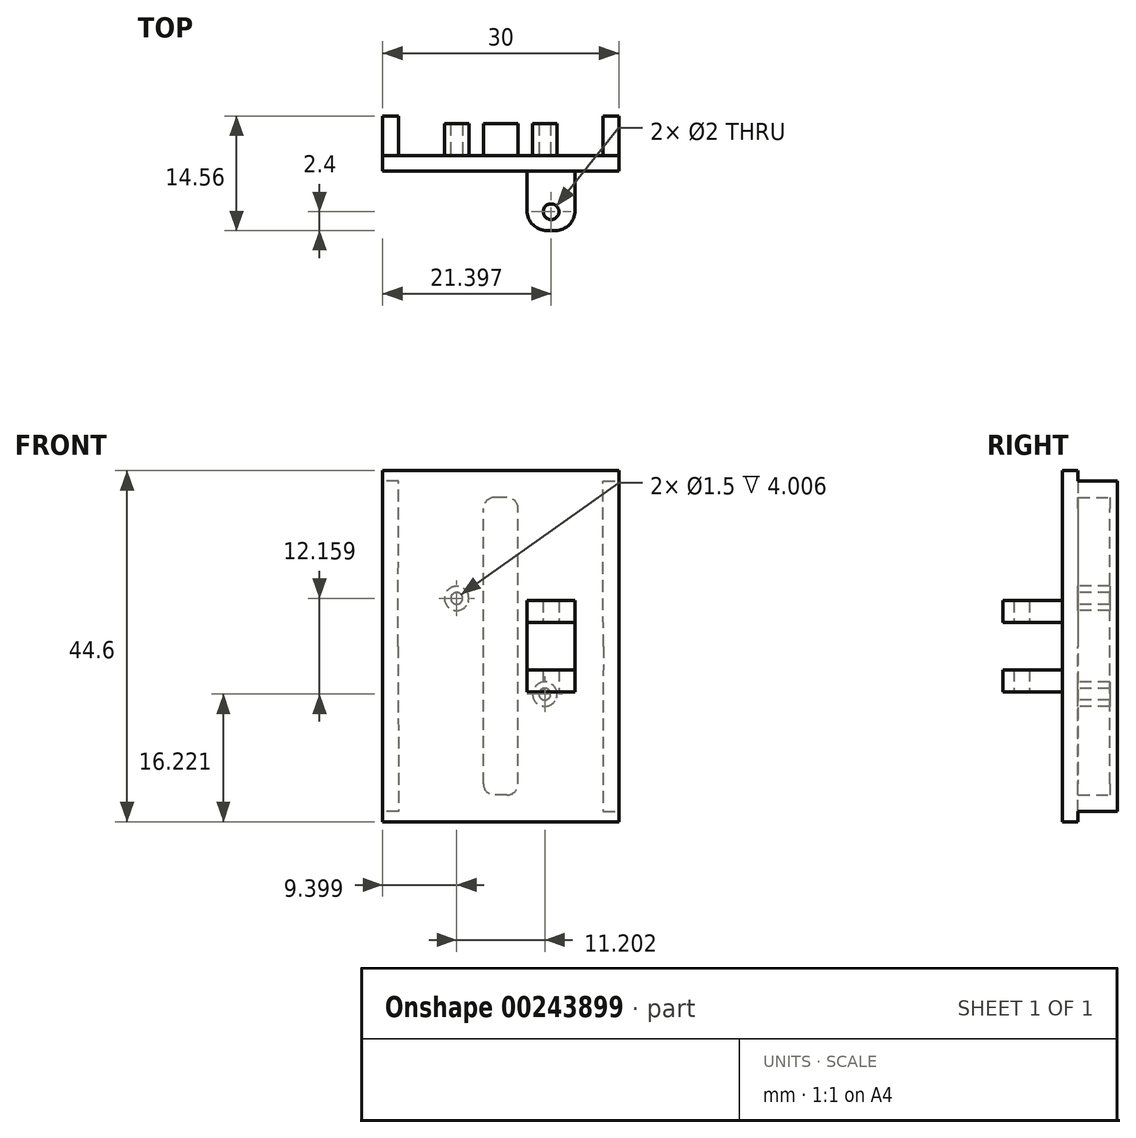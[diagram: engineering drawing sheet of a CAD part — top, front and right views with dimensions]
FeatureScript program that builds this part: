
annotation { "Feature Type Name" : "Feature", "Feature Type Description" : "" }
export const myFeature = defineFeature(function(context is Context, id is Id, definition is map)
    precondition{}
    {
        {
            var Q0;
            Q0=qCreatedBy(makeId("Front.planeOp"),FACE);
            var sketch = newSketch(context, id + "F0", { "sketchPlane" : qUnion([Q0])});
            skLineSegment(sketch, "E0.bottom", {"start": v(15, 22.3) * mm, "end": v(-15, 22.3) * mm});
            skLineSegment(sketch, "E0.top", {"start": v(15, -22.3) * mm, "end": v(-15, -22.3) * mm});
            skLineSegment(sketch, "E0.left", {"start": v(15, 22.3) * mm, "end": v(15, -22.3) * mm});
            skLineSegment(sketch, "E0.right", {"start": v(-15, 22.3) * mm, "end": v(-15, -22.3) * mm});
            skSolve(sketch);
        }
        {
            var Q0;
            Q0=makeQuery(id+"F0.imprint","IMPRINT",FACE,{"disambiguationData":[TD([[makeQuery(id+"F0.imprint","IMPRINT",EDGE,{"derivedFrom":sQuery(id+"F0.wireOp",EDGE,"E0.bottom")}),1.0]])]});
            extrude(context, id + "F1", {"entities" : qUnion([Q0]), "depth" : 8 * mm});
        }
        {
            var Q0;
            Q0=makeQuery(id+"F0.imprint","IMPRINT",FACE,{"disambiguationData":[TD([[makeQuery(id+"F0.imprint","IMPRINT",EDGE,{"derivedFrom":sQuery(id+"F0.wireOp",EDGE,"E0.bottom")}),1.0]])]});
            var sketch = newSketch(context, id + "F2", { "sketchPlane" : qUnion([Q0])});
            skLineSegment(sketch, "E1.0", {"start": v(15, 22.3) * mm, "end": v(0, 22.3) * mm});
            skLineSegment(sketch, "E2.0", {"start": v(15, 22.3) * mm, "end": v(15, 20.99) * mm});
            skLineSegment(sketch, "E3.top", {"start": v(15, 20.99) * mm, "end": v(13, 20.99) * mm});
            skPoint(sketch, "E4", {"position": v(15, 20.99) * mm});
            skLineSegment(sketch, "E5", {"start": v(13, 20.99) * mm, "end": v(13.02, 0) * mm});
            skLineSegment(sketch, "E6.bottom", {"start": v(-0.8, 18.9) * mm, "end": v(0.8, 18.9) * mm});
            skLineSegment(sketch, "E6.top", {"start": v(-0.8, -18.9) * mm, "end": v(0.8, -18.9) * mm});
            skLineSegment(sketch, "E6.left", {"start": v(-2.2, 17.5) * mm, "end": v(-2.2, -17.5) * mm});
            skLineSegment(sketch, "E6.right", {"start": v(2.2, 17.5) * mm, "end": v(2.2, -17.5) * mm});
            skPoint(sketch, "E6.middle", {"position": v(0, 0) * mm});
            skPoint(sketch, "E7.visualSharp", {"position": v(2.2, 18.9) * mm});
            skArc(sketch, "E7.filletArc", {"start": v(2.2, 17.5) * mm, "mid": v(1.8, 18.5) * mm, "end": v(0.8, 18.9) * mm});
            skPoint(sketch, "E8.visualSharp", {"position": v(-2.2, 18.9) * mm});
            skArc(sketch, "E8.filletArc", {"start": v(-0.8, 18.9) * mm, "mid": v(-1.8, 18.5) * mm, "end": v(-2.2, 17.5) * mm});
            skPoint(sketch, "E9.visualSharp", {"position": v(2.2, -18.9) * mm});
            skArc(sketch, "E9.filletArc", {"start": v(0.8, -18.9) * mm, "mid": v(1.8, -18.5) * mm, "end": v(2.2, -17.5) * mm});
            skPoint(sketch, "E10.visualSharp", {"position": v(-2.2, -18.9) * mm});
            skArc(sketch, "E10.filletArc", {"start": v(-2.2, -17.5) * mm, "mid": v(-1.8, -18.5) * mm, "end": v(-0.8, -18.9) * mm});
            skLineSegment(sketch, "E11.MirrorCS", {"start": v(-15, 22.3) * mm, "end": v(0, 22.3) * mm});
            skLineSegment(sketch, "E12.MirrorCS", {"start": v(-13, 20.99) * mm, "end": v(-13.02, 0) * mm});
            skLineSegment(sketch, "E13.MirrorCS", {"start": v(-15, 22.3) * mm, "end": v(-15, 20.99) * mm});
            skLineSegment(sketch, "E14.MirrorCS", {"start": v(-15, 20.99) * mm, "end": v(-13, 20.99) * mm});
            skLineSegment(sketch, "E15.MirrorCS", {"start": v(13, -20.99) * mm, "end": v(13.02, 0) * mm});
            skLineSegment(sketch, "E16.MirrorCS", {"start": v(15, -20.99) * mm, "end": v(13, -20.99) * mm});
            skLineSegment(sketch, "E17.MirrorCS", {"start": v(15, -22.3) * mm, "end": v(0, -22.3) * mm});
            skLineSegment(sketch, "E18.MirrorCS", {"start": v(-15, -22.3) * mm, "end": v(0, -22.3) * mm});
            skLineSegment(sketch, "E19.MirrorCS", {"start": v(-13, -20.99) * mm, "end": v(-13.02, 0) * mm});
            skLineSegment(sketch, "E20.MirrorCS", {"start": v(-15, -20.99) * mm, "end": v(-13, -20.99) * mm});
            skLineSegment(sketch, "E21.MirrorCS", {"start": v(-15, -22.3) * mm, "end": v(-15, -20.99) * mm});
            skLineSegment(sketch, "E22.MirrorCS", {"start": v(15, -22.3) * mm, "end": v(15, -20.99) * mm});
            skSolve(sketch);
        }
        {
            var Q0;
            Q0=makeQuery(id+"F2.imprint","IMPRINT",FACE,{"disambiguationData":[TD([[makeQuery(id+"F2.imprint","IMPRINT",EDGE,{"derivedFrom":sQuery(id+"F2.wireOp",EDGE,"E1.0")}),1.0]])]});
            extrude(context, id + "F3", {"entities" : qUnion([Q0]), "operationType" : NewBodyOperationType.REMOVE, "depth" : 6 * mm});
        }
        {
            var Q0;
            Q0=qCreatedBy(makeId("Top.planeOp"),FACE);
            var sketch = newSketch(context, id + "F4", { "sketchPlane" : qUnion([Q0])});
            skLineSegment(sketch, "E23.bottom", {"start": v(10.41, 0) * mm, "end": v(-10.59, 0) * mm});
            skLineSegment(sketch, "E23.top", {"start": v(10.41, -2) * mm, "end": v(-10.59, -2) * mm});
            skLineSegment(sketch, "E23.left", {"start": v(10.41, 0) * mm, "end": v(10.41, -2) * mm});
            skLineSegment(sketch, "E23.right", {"start": v(-10.59, 0) * mm, "end": v(-10.59, -2) * mm});
            skSolve(sketch);
        }
        {
            var Q0;
            Q0=makeQuery(id+"F1.opExtrude","CAP_FACE",FACE,{"disambiguationData":[OSD([sQuery(id+"F0.wireOp",EDGE,"E0.bottom"),sQuery(id+"F0.wireOp",EDGE,"E0.top"),sQuery(id+"F0.wireOp",EDGE,"E0.left"),sQuery(id+"F0.wireOp",EDGE,"E0.right")])],"isStart":false});
            var sketch = newSketch(context, id + "F5", { "sketchPlane" : qUnion([Q0])});
            skLineSegment(sketch, "E24.0.0", {"start": v(3.35, -5.78) * mm, "end": v(9.45, -5.78) * mm});
            skLineSegment(sketch, "E24.0.1", {"start": v(9.45, -5.78) * mm, "end": v(9.45, 5.82) * mm});
            skLineSegment(sketch, "E24.0.2", {"start": v(9.45, 5.82) * mm, "end": v(3.35, 5.82) * mm});
            skLineSegment(sketch, "E24.0.3", {"start": v(3.35, 5.82) * mm, "end": v(3.35, -5.78) * mm});
            skSolve(sketch);
        }
        {
            var Q0;
            Q0=makeQuery(id+"F5.imprint","IMPRINT",FACE,{"disambiguationData":[TD([[makeQuery(id+"F5.imprint","IMPRINT",EDGE,{"derivedFrom":sQuery(id+"F5.wireOp",EDGE,"E24.0.0")}),1.0]])]});
            extrude(context, id + "F6", {"entities" : qUnion([Q0]), "operationType" : NewBodyOperationType.ADD, "depth" : 7.56 * mm});
        }
        {
            var Q0;
            Q0=makeQuery(id+"F6.opExtrude","CAP_EDGE",EDGE,{"disambiguationData":[OSD([sQuery(id+"F5.wireOp",EDGE,"E24.0.3")])],"isStart":false});
            var Q1;
            Q1=makeQuery(id+"F6.opExtrude","CAP_EDGE",EDGE,{"disambiguationData":[OSD([sQuery(id+"F5.wireOp",EDGE,"E24.0.1")])],"isStart":false});
            fillet(context, id + "F7", {"entities" : qUnion([Q0, Q1]), "radius" : 2.53 * mm, "tangentPropagation" : true, "allowEdgeOverflow" : false});
        }
        {
            var Q0;
            Q0=qCreatedBy(makeId("Top.planeOp"),FACE);
            var sketch = newSketch(context, id + "F8", { "sketchPlane" : qUnion([Q0])});
            skCircle(sketch, "E25", {"center": v(6.4, -13.16) * mm, "radius": 1 * mm});
            skSolve(sketch);
        }
        {
            var Q0;
            Q0 = qSketchRegion(id + "F8", true);
            extrude(context, id + "F9", {"entities" : qUnion([Q0]), "operationType" : NewBodyOperationType.REMOVE, "endBound" : BoundingType.SYMMETRIC, "depth" : 25 * mm});
        }
        {
            var Q0;
            Q0=qCreatedBy(makeId("Right.planeOp"),FACE);
            var sketch = newSketch(context, id + "F10", { "sketchPlane" : qUnion([Q0])});
            skLineSegment(sketch, "E26.bottom", {"start": v(-16.02, 3) * mm, "end": v(-8.02, 3) * mm});
            skLineSegment(sketch, "E26.top", {"start": v(-16.02, -3) * mm, "end": v(-8.02, -3) * mm});
            skLineSegment(sketch, "E26.left", {"start": v(-16.02, 3) * mm, "end": v(-16.02, -3) * mm});
            skLineSegment(sketch, "E26.right", {"start": v(-8.02, 3) * mm, "end": v(-8.02, -3) * mm});
            skPoint(sketch, "E26.middle", {"position": v(-12.02, 0) * mm});
            skSolve(sketch);
        }
        {
            var Q0;
            Q0=makeQuery(id+"F10.imprint","IMPRINT",FACE,{"disambiguationData":[TD([[makeQuery(id+"F10.imprint","IMPRINT",EDGE,{"derivedFrom":sQuery(id+"F10.wireOp",EDGE,"E26.bottom")}),-1.0]])]});
            extrude(context, id + "F11", {"entities" : qUnion([Q0]), "operationType" : NewBodyOperationType.REMOVE, "endBound" : BoundingType.SYMMETRIC, "depth" : 25 * mm});
        }
        {
            var Q0;
            Q0=qCreatedBy(makeId("Top.planeOp"),FACE);
            var sketch = newSketch(context, id + "F12", { "sketchPlane" : qUnion([Q0])});
            skLineSegment(sketch, "E27.bottom", {"start": v(-15.26, 0) * mm, "end": v(15.9, 0) * mm});
            skLineSegment(sketch, "E27.top", {"start": v(-15.26, -1) * mm, "end": v(15.9, -1) * mm});
            skLineSegment(sketch, "E27.left", {"start": v(-15.26, 0) * mm, "end": v(-15.26, -1) * mm});
            skLineSegment(sketch, "E27.right", {"start": v(15.9, 0) * mm, "end": v(15.9, -1) * mm});
            skSolve(sketch);
        }
        {
            var Q0;
            Q0=makeQuery(id+"F12.imprint","IMPRINT",FACE,{"disambiguationData":[TD([[makeQuery(id+"F12.imprint","IMPRINT",EDGE,{"derivedFrom":sQuery(id+"F12.wireOp",EDGE,"E27.bottom")}),-1.0]])]});
            extrude(context, id + "F13", {"entities" : qUnion([Q0]), "operationType" : NewBodyOperationType.REMOVE, "endBound" : BoundingType.SYMMETRIC, "depth" : 52.4 * mm});
        }
        {
            var Q0;
            Q0=qCreatedBy(makeId("Front.planeOp"),FACE);
            cPlane(context, id + "F14", {"entities" : qUnion([Q0]), "cplaneType" : CPlaneType.OFFSET, "offset" : 6 * mm, "width" : 150 * mm, "height" : 150 * mm});
        }
        {
            var Q0;
            Q0=qCreatedBy(id+"F14.planeOp",FACE);
            var sketch = newSketch(context, id + "F15", { "sketchPlane" : qUnion([Q0])});
            skCircle(sketch, "E28.MirrorC", {"center": v(5.6, -6.08) * mm, "radius": 0.75 * mm});
            skCircle(sketch, "E29.MirrorC", {"center": v(5.6, -6.08) * mm, "radius": 1.55 * mm});
            skCircle(sketch, "E30.MirrorC", {"center": v(-5.6, 6.08) * mm, "radius": 1.55 * mm});
            skCircle(sketch, "E31.MirrorC", {"center": v(-5.6, 6.08) * mm, "radius": 0.75 * mm});
            skSolve(sketch);
        }
        {
            var Q0;
            Q0 = qSketchRegion(id + "F15", true);
            extrude(context, id + "F16", {"entities" : qUnion([Q0]), "operationType" : NewBodyOperationType.ADD, "oppositeDirection" : true, "depth" : 4.95 * mm});
        }
        {
            var Q0;
            Q0=makeQuery(id+"F4.imprint","IMPRINT",FACE,{"disambiguationData":[TD([[makeQuery(id+"F4.imprint","IMPRINT",EDGE,{"derivedFrom":sQuery(id+"F4.wireOp",EDGE,"E23.bottom")}),1.0]])]});
            extrude(context, id + "F17", {"entities" : qUnion([Q0]), "operationType" : NewBodyOperationType.REMOVE, "endBound" : BoundingType.SYMMETRIC, "oppositeDirection" : true, "depth" : 93 * mm});
        }
    });
